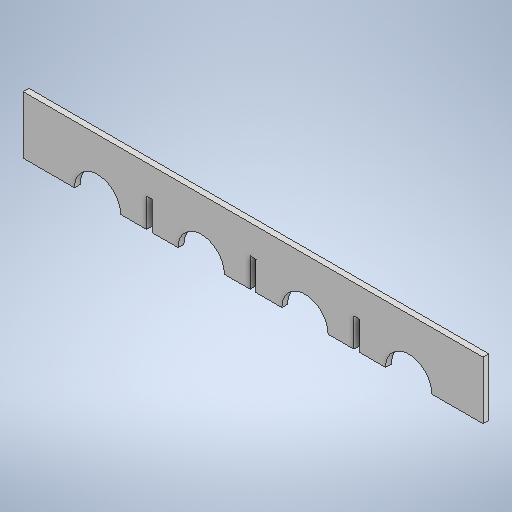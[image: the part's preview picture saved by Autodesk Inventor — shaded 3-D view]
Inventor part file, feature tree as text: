
AUTODESK INVENTOR PART (.ipt)
format: ipt  version: 2025 (Build 290162010, 162A)  size: 295,424 bytes
history: native  units: mm
features: extrude x2, sketch x2
ambient origin geometry x8: Origin, YZ Plane, XZ Plane, XY Plane, X Axis, Y Axis, Z Axis, Center Point
bodies: Solid1 (feature_tree)
feature tree (4):
  extrude  "Extrusion1"  Depth=10.0mm
  extrude  "Extrusion2"  Depth=100.0mm TaperAngle=0.0deg
  sketch  "Sketch1"  dims[d0=800.0mm d1=10.0mm]
  sketch  "Sketch2"  dims[d2=798.0mm d3=100.0mm d4=0.0mm d5=80.0mm d7=90.0mm d8=80.0mm d9=180.0mm d10=80.0mm d11=80.0mm d12=90.0mm d13=180.0mm d22=0.0mm d23=0.0mm d24=10.0mm d25=50.0mm d26=10.0mm d27=50.0mm d28=180.0mm d29=10.0mm d30=50.0mm d31=180.0mm]
